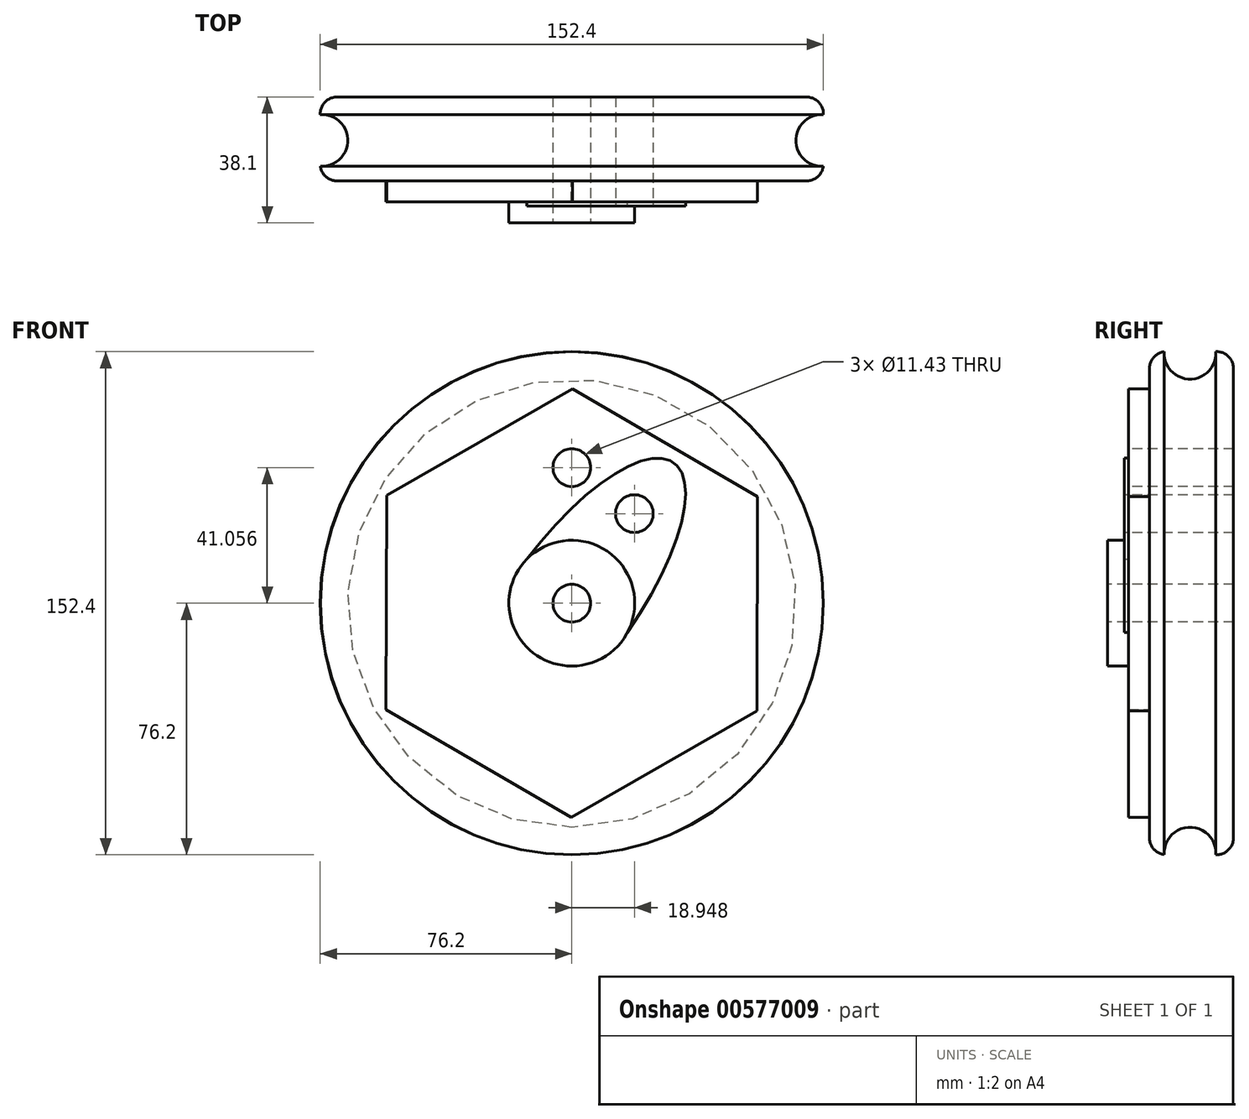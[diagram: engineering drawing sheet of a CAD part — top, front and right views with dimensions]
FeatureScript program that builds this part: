
annotation { "Feature Type Name" : "Feature", "Feature Type Description" : "" }
export const myFeature = defineFeature(function(context is Context, id is Id, definition is map)
    precondition{}
    {
        {
            var Q0;
            Q0=qCreatedBy(makeId("Front.planeOp"),FACE);
            var sketch = newSketch(context, id + "F0", { "sketchPlane" : qUnion([Q0])});
            skCircle(sketch, "E0", {"center": v(0, 0) * mm, "radius": 76.2 * mm});
            skSolve(sketch);
        }
        {
            var Q0;
            Q0=makeQuery(id+"F0.imprint","IMPRINT",FACE,{"disambiguationData":[TD([[makeQuery(id+"F0.imprint","IMPRINT",EDGE,{"derivedFrom":sQuery(id+"F0.wireOp",EDGE,"E0")}),1.0]])]});
            extrude(context, id + "F1", {"entities" : qUnion([Q0]), "depth" : 25.4 * mm, "offsetDistance" : 25.4 * mm});
        }
        {
            var Q0;
            Q0=makeQuery(id+"F1.opExtrude","CAP_FACE",FACE,{"disambiguationData":[OSD([sQuery(id+"F0.wireOp",EDGE,"E0")])],"isStart":false});
            var sketch = newSketch(context, id + "F2", { "sketchPlane" : qUnion([Q0])});
            skCircle(sketch, "E1", {"center": v(0, 0) * mm, "radius": 19.05 * mm});
            skSolve(sketch);
        }
        {
            var Q0;
            Q0=makeQuery(id+"F2.imprint","IMPRINT",FACE,{"disambiguationData":[TD([[makeQuery(id+"F2.imprint","IMPRINT",EDGE,{"derivedFrom":sQuery(id+"F2.wireOp",EDGE,"E1")}),1.0]])]});
            extrude(context, id + "F3", {"entities" : qUnion([Q0]), "operationType" : NewBodyOperationType.ADD, "depth" : 12.7 * mm, "offsetDistance" : 25.4 * mm});
        }
        {
            var Q0;
            Q0=makeQuery(id+"F3.opExtrude","CAP_FACE",FACE,{"disambiguationData":[OSD([sQuery(id+"F2.wireOp",EDGE,"E1")])],"isStart":false});
            var sketch = newSketch(context, id + "F4", { "sketchPlane" : qUnion([Q0])});
            skPoint(sketch, "E2", {"position": v(0, 0) * mm});
            skSolve(sketch);
        }
        {
            var Q0;
            Q0=sQuery(id+"F4.wireOp",VERTEX,"E2");
            var Q1;
            Q1=makeQuery(id+"F1.opExtrude","SWEPT_BODY",BODY,{"disambiguationData":[OSD([sQuery(id+"F0.wireOp",EDGE,"E0")])]});
            hole(context, id + "F5", {"style" : HoleStyle.SIMPLE, "endStyle" : HoleEndStyle.THROUGH, "holeDiameter" : 11.43 * mm, "isTappedThrough" : true, "tappedDepth" : 12.7 * mm, "tapClearance" : 3, "locations" : qUnion([Q0]), "scope" : qUnion([Q1])});
        }
        {
            var Q0;
            Q0=makeQuery(id+"F1.opExtrude","SWEPT_FACE",FACE,{"disambiguationData":[OSD([sQuery(id+"F0.wireOp",EDGE,"E0")])]});
            fillet(context, id + "F6", {"entities" : qUnion([Q0]), "radius" : 5.08 * mm, "tangentPropagation" : true, "allowEdgeOverflow" : false});
        }
        {
            var Q0;
            Q0=makeQuery(id+"F1.opExtrude","CAP_FACE",FACE,{"disambiguationData":[OSD([sQuery(id+"F0.wireOp",EDGE,"E0")])],"isStart":false});
            var sketch = newSketch(context, id + "F7", { "sketchPlane" : qUnion([Q0])});
            skCircle(sketch, "E3.cCircle", {"center": v(0, 0) * mm, "radius": 56.17 * mm, "construction": true});
            skLineSegment(sketch, "E3.0", {"start": v(0.2, 64.86) * mm, "end": v(56.27, 32.26) * mm});
            skLineSegment(sketch, "E3.1", {"start": v(56.27, 32.26) * mm, "end": v(56.07, -32.6) * mm});
            skLineSegment(sketch, "E3.2", {"start": v(56.07, -32.6) * mm, "end": v(-0.2, -64.86) * mm});
            skLineSegment(sketch, "E3.3", {"start": v(-0.2, -64.86) * mm, "end": v(-56.27, -32.26) * mm});
            skLineSegment(sketch, "E3.4", {"start": v(-56.27, -32.26) * mm, "end": v(-56.07, 32.6) * mm});
            skLineSegment(sketch, "E3.5", {"start": v(-56.07, 32.6) * mm, "end": v(0.2, 64.86) * mm});
            skPoint(sketch, "E3.0.midPoint", {"position": v(28.23, 48.56) * mm});
            skSolve(sketch);
        }
        {
            var Q0;
            Q0=makeQuery(id+"F7.imprint","IMPRINT",FACE,{"disambiguationData":[TD([[makeQuery(id+"F7.imprint","IMPRINT",EDGE,{"derivedFrom":sQuery(id+"F7.wireOp",EDGE,"E3.0")}),-1.0]])]});
            extrude(context, id + "F8", {"entities" : qUnion([Q0]), "operationType" : NewBodyOperationType.ADD, "depth" : 6.35 * mm, "offsetDistance" : 25.4 * mm});
        }
        {
            var Q0;
            Q0=makeQuery(id+"F8.opExtrude","CAP_FACE",FACE,{"disambiguationData":[OSD([sQuery(id+"F2.wireOp",EDGE,"E1"),sQuery(id+"F7.wireOp",EDGE,"E3.0"),sQuery(id+"F7.wireOp",EDGE,"E3.1"),sQuery(id+"F7.wireOp",EDGE,"E3.2"),sQuery(id+"F7.wireOp",EDGE,"E3.3"),sQuery(id+"F7.wireOp",EDGE,"E3.4"),sQuery(id+"F7.wireOp",EDGE,"E3.5")])],"isStart":false});
            var sketch = newSketch(context, id + "F9", { "sketchPlane" : qUnion([Q0])});
            skEllipse(sketch, "E4", {"center": v(0, 0) * mm, "majorRadius": 52.59 * mm, "minorRadius": 18.87 * mm, "majorAxis": v(0.59, 0.8)});
            skSolve(sketch);
        }
        {
            var Q0;
            Q0=qCreatedBy(makeId("Right.planeOp"),FACE);
            var sketch = newSketch(context, id + "F10", { "sketchPlane" : qUnion([Q0])});
            skCircle(sketch, "E5", {"center": v(-13.14, 75.69) * mm, "radius": 7.82 * mm});
            skPoint(sketch, "E5.first.point", {"position": v(-20.92, 76.53) * mm});
            skPoint(sketch, "E5.second.point", {"position": v(-5.32, 75.66) * mm});
            skPoint(sketch, "E5.third.point", {"position": v(-13.12, 67.86) * mm});
            skSolve(sketch);
        }
        {
            var Q0;
            Q0=makeQuery(id+"F10.imprint","IMPRINT",FACE,{"disambiguationData":[TD([[makeQuery(id+"F10.imprint","IMPRINT",EDGE,{"derivedFrom":sQuery(id+"F10.wireOp",EDGE,"E5")}),1.0]])]});
            var Q1;
            Q1=sQuery(id+"F10.wireOp",EDGE,"E5");
            var Q2;
            Q2=makeQuery(id+"F1.opExtrude","SWEPT_FACE",FACE,{"disambiguationData":[OSD([sQuery(id+"F0.wireOp",EDGE,"E0")])]});
            revolve(context, id + "F11", {"operationType" : NewBodyOperationType.REMOVE, "entities" : qUnion([Q0]), "surfaceEntities" : qUnion([Q1]), "axis" : qUnion([Q2]), "revolveType" : RevolveType.FULL, "oppositeDirection" : true});
        }
        {
            var Q0;
            {var subQ0=sQuery(id+"F9.wireOp",EDGE,"E4");var subQ1=makeQuery(id+"F8.opExtrude","CAP_EDGE",EDGE,{"disambiguationData":[OSD([sQuery(id+"F2.wireOp",EDGE,"E1")])],"isStart":false});var subQ2=makeQuery(id+"F9.imprint","INTERSECT",VERTEX,{"disambiguationData":[OD(1.0)],"derivedFrom":[subQ1,subQ0]});Q0=makeQuery(id+"F9.imprint","IMPRINT",FACE,{"disambiguationData":[TD([[makeQuery(id+"F9.imprint","IMPRINT",EDGE,{"disambiguationData":[TD([[subQ2,1.0]])],"derivedFrom":subQ0}),1.0]])]});}
            extrude(context, id + "F12", {"entities" : qUnion([Q0]), "operationType" : NewBodyOperationType.ADD, "depth" : 1.27 * mm, "offsetDistance" : 25.4 * mm});
        }
        {
            var Q0;
            Q0=makeQuery(id+"F12.opExtrude","CAP_FACE",FACE,{"disambiguationData":[OSD([sQuery(id+"F2.wireOp",EDGE,"E1"),sQuery(id+"F9.wireOp",EDGE,"E4")])],"isStart":false});
            var sketch = newSketch(context, id + "F13", { "sketchPlane" : qUnion([Q0])});
            skPoint(sketch, "E6", {"position": v(18.95, 27.13) * mm});
            skSolve(sketch);
        }
        {
            var Q0;
            Q0=sQuery(id+"F13.wireOp",VERTEX,"E6");
            var Q1;
            Q1=makeQuery(id+"F1.opExtrude","SWEPT_BODY",BODY,{"disambiguationData":[OSD([sQuery(id+"F0.wireOp",EDGE,"E0")])]});
            hole(context, id + "F14", {"style" : HoleStyle.SIMPLE, "endStyle" : HoleEndStyle.THROUGH, "holeDiameter" : 11.43 * mm, "majorDiameter" : 6.35 * mm, "isTappedThrough" : true, "tappedDepth" : 12.7 * mm, "tapClearance" : 3, "locations" : qUnion([Q0]), "scope" : qUnion([Q1])});
        }
        {
            var Q0;
            Q0=makeQuery(id+"F8.opExtrude","CAP_FACE",FACE,{"disambiguationData":[OSD([sQuery(id+"F2.wireOp",EDGE,"E1"),sQuery(id+"F7.wireOp",EDGE,"E3.0"),sQuery(id+"F7.wireOp",EDGE,"E3.1"),sQuery(id+"F7.wireOp",EDGE,"E3.2"),sQuery(id+"F7.wireOp",EDGE,"E3.3"),sQuery(id+"F7.wireOp",EDGE,"E3.4"),sQuery(id+"F7.wireOp",EDGE,"E3.5")])],"isStart":false});
            var sketch = newSketch(context, id + "F15", { "sketchPlane" : qUnion([Q0])});
            skPoint(sketch, "E7", {"position": v(0, 41.06) * mm});
            skSolve(sketch);
        }
        {
            var Q0;
            Q0=sQuery(id+"F15.wireOp",VERTEX,"E7");
            var Q1;
            Q1=makeQuery(id+"F1.opExtrude","SWEPT_BODY",BODY,{"disambiguationData":[OSD([sQuery(id+"F0.wireOp",EDGE,"E0")])]});
            hole(context, id + "F16", {"style" : HoleStyle.SIMPLE, "endStyle" : HoleEndStyle.THROUGH, "holeDiameter" : 11.43 * mm, "majorDiameter" : 6.35 * mm, "isTappedThrough" : true, "tappedDepth" : 12.7 * mm, "tapClearance" : 3, "locations" : qUnion([Q0]), "scope" : qUnion([Q1])});
        }
    });
